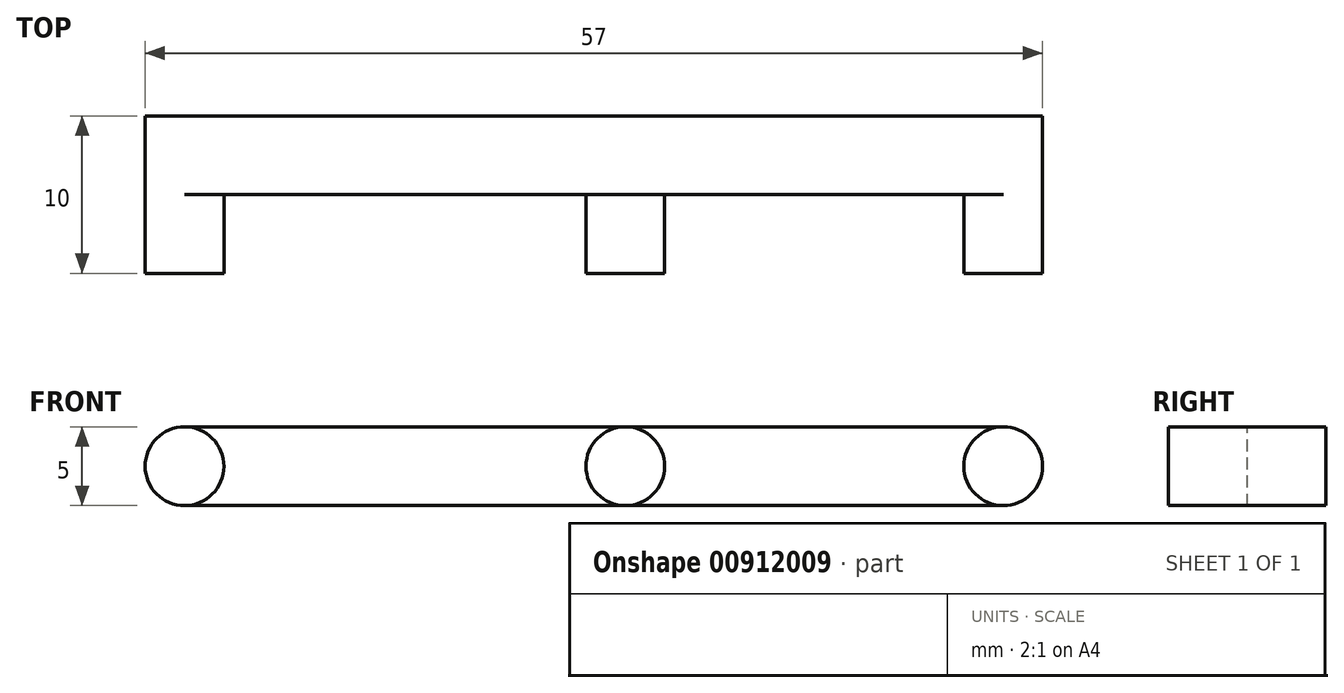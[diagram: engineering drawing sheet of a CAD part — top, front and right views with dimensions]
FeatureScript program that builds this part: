
annotation { "Feature Type Name" : "Feature", "Feature Type Description" : "" }
export const myFeature = defineFeature(function(context is Context, id is Id, definition is map)
    precondition{}
    {
        {
            var Q0;
            Q0=qCreatedBy(makeId("Front.planeOp"),FACE);
            var sketch = newSketch(context, id + "F0", { "sketchPlane" : qUnion([Q0])});
            skCircle(sketch, "E0", {"center": v(0, 0) * mm, "radius": 2.5 * mm});
            skCircle(sketch, "E1", {"center": v(28, 0) * mm, "radius": 2.5 * mm});
            skCircle(sketch, "E2", {"center": v(52, 0) * mm, "radius": 2.5 * mm});
            skLineSegment(sketch, "E3.bottom", {"start": v(0, 2.5) * mm, "end": v(52, 2.5) * mm});
            skLineSegment(sketch, "E3.top", {"start": v(0, -2.5) * mm, "end": v(52, -2.5) * mm});
            skLineSegment(sketch, "E3.left", {"start": v(0, 2.5) * mm, "end": v(0, -2.5) * mm});
            skLineSegment(sketch, "E3.right", {"start": v(52, 2.5) * mm, "end": v(52, -2.5) * mm});
            skSolve(sketch);
        }
        {
            var Q0;
            {var subQ0=sQuery(id+"F0.wireOp",EDGE,"E3.left");Q0=makeQuery(id+"F0.imprint","IMPRINT",FACE,{"disambiguationData":[TD([[makeQuery(id+"F0.imprint","IMPRINT",EDGE,{"derivedFrom":subQ0}),1.0]])]});}
            var Q1;
            {var subQ0=sQuery(id+"F0.wireOp",EDGE,"E1");var subQ1=makeQuery(id+"F0.imprint","INTERSECT",VERTEX,{"derivedFrom":[subQ0,sQuery(id+"F0.wireOp",EDGE,"E3.bottom")]});Q1=makeQuery(id+"F0.imprint","IMPRINT",FACE,{"disambiguationData":[TD([[makeQuery(id+"F0.imprint","IMPRINT",EDGE,{"disambiguationData":[TD([[subQ1,-1.0]])],"derivedFrom":subQ0}),1.0]])]});}
            var Q2;
            {var subQ0=sQuery(id+"F0.wireOp",EDGE,"E3.right");Q2=makeQuery(id+"F0.imprint","IMPRINT",FACE,{"disambiguationData":[TD([[makeQuery(id+"F0.imprint","IMPRINT",EDGE,{"derivedFrom":subQ0}),1.0]])]});}
            var Q3;
            {var subQ0=sQuery(id+"F0.wireOp",EDGE,"E3.right");Q3=makeQuery(id+"F0.imprint","IMPRINT",FACE,{"disambiguationData":[TD([[makeQuery(id+"F0.imprint","IMPRINT",EDGE,{"derivedFrom":subQ0}),-1.0]])]});}
            var Q4;
            {var subQ0=sQuery(id+"F0.wireOp",EDGE,"E3.left");Q4=makeQuery(id+"F0.imprint","IMPRINT",FACE,{"disambiguationData":[TD([[makeQuery(id+"F0.imprint","IMPRINT",EDGE,{"derivedFrom":subQ0}),-1.0]])]});}
            extrude(context, id + "F1", {"entities" : qUnion([Q0, Q1, Q2, Q3, Q4]), "depth" : 10 * mm, "offsetDistance" : 25 * mm});
        }
        {
            var Q0;
            Q0 = qSketchRegion(id + "F0", true);
            extrude(context, id + "F2", {"entities" : qUnion([Q0]), "operationType" : NewBodyOperationType.ADD, "depth" : 5 * mm, "offsetDistance" : 25 * mm});
        }
    });
